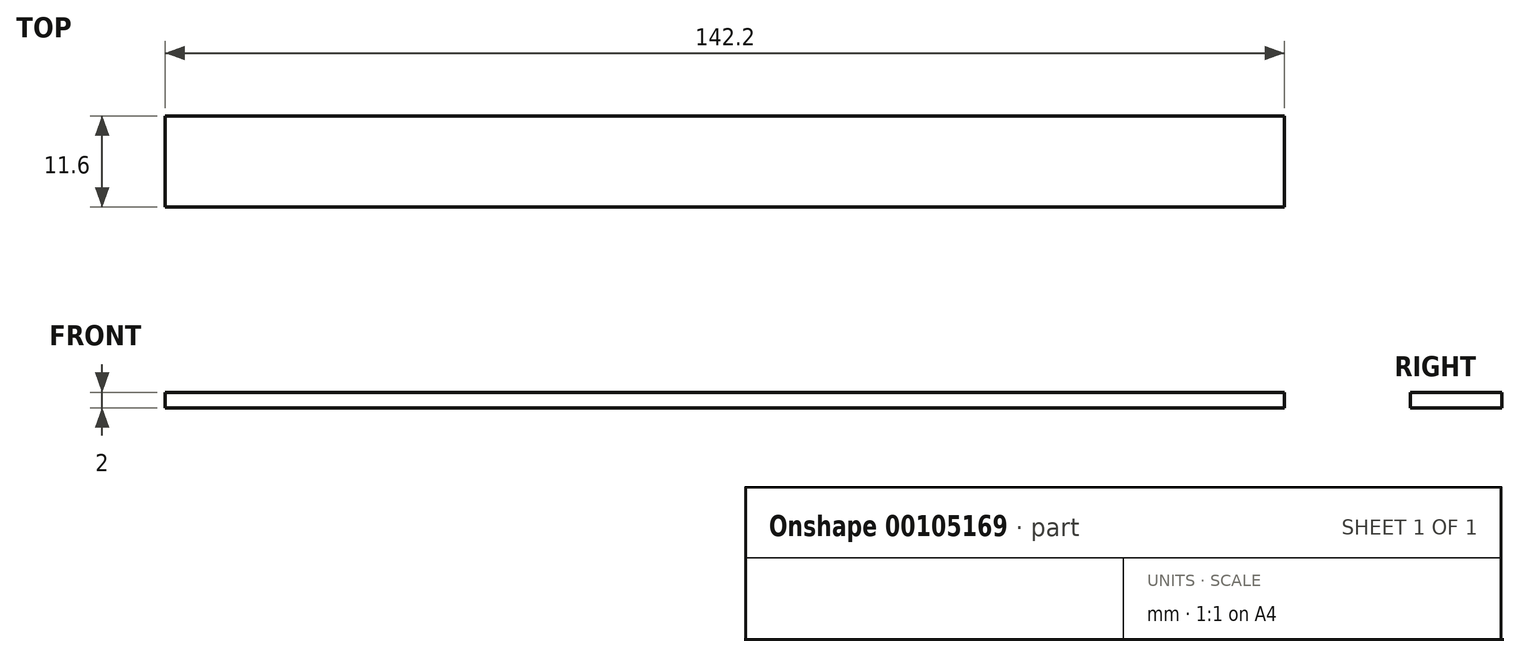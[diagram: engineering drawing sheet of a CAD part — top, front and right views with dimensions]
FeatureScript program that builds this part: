
annotation { "Feature Type Name" : "Feature", "Feature Type Description" : "" }
export const myFeature = defineFeature(function(context is Context, id is Id, definition is map)
    precondition{}
    {
        {
            var Q0;
            Q0=qCreatedBy(makeId("Top.planeOp"),FACE);
            var sketch = newSketch(context, id + "F0", { "sketchPlane" : qUnion([Q0])});
            skLineSegment(sketch, "E0.bottom", {"start": v(-72.84, 7.77) * mm, "end": v(69.36, 7.77) * mm});
            skLineSegment(sketch, "E0.top", {"start": v(-72.84, -3.83) * mm, "end": v(69.36, -3.83) * mm});
            skLineSegment(sketch, "E0.left", {"start": v(-72.84, 7.77) * mm, "end": v(-72.84, -3.83) * mm});
            skLineSegment(sketch, "E0.right", {"start": v(69.36, 7.77) * mm, "end": v(69.36, -3.83) * mm});
            skSolve(sketch);
        }
        {
            var Q0;
            Q0 = qSketchRegion(id + "F0", true);
            extrude(context, id + "F1", {"entities" : qUnion([Q0]), "depth" : 2 * mm});
        }
    });
